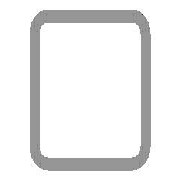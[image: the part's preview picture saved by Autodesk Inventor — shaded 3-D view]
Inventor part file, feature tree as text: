
AUTODESK INVENTOR PART (.ipt)
format: ipt  version: 2025.3 (Build 293356000, 356)  size: 145,920 bytes
history: native  units: mm (DEFAULTED — no unit token found)
features: other x4, plane x3, split x2, sketch x1
ambient origin geometry x8: Origin, YZ Plane, XZ Plane, XY Plane, X Axis, Y Axis, Z Axis, Center Point
bodies: Solid1 (feature_tree), Body (feature_tree)
feature tree (10):
  parser-record x1  (decoder bookkeeping rows leaked as tree rows — omitted from the tree; the rows remain in map.json)
  other  "Driven Length"
  other  "Start Plane"
  other  "End Plane"
  plane  "Work Plane4"
  split  "Split1"
  plane  "Work Plane5"
  split  "Split2"
  sketch  "Sketch3"  dims[d3=2559.340203mm d4=0.0mm d7=6.0mm d9=80.0mm d11=80.0mm d12=3.0mm d13=80.0mm d14=2639.340203mm d15=40.0mm d16=40.0mm d17=90.0deg d18=2559.340203mm]
  plane  "Work Plane3"
